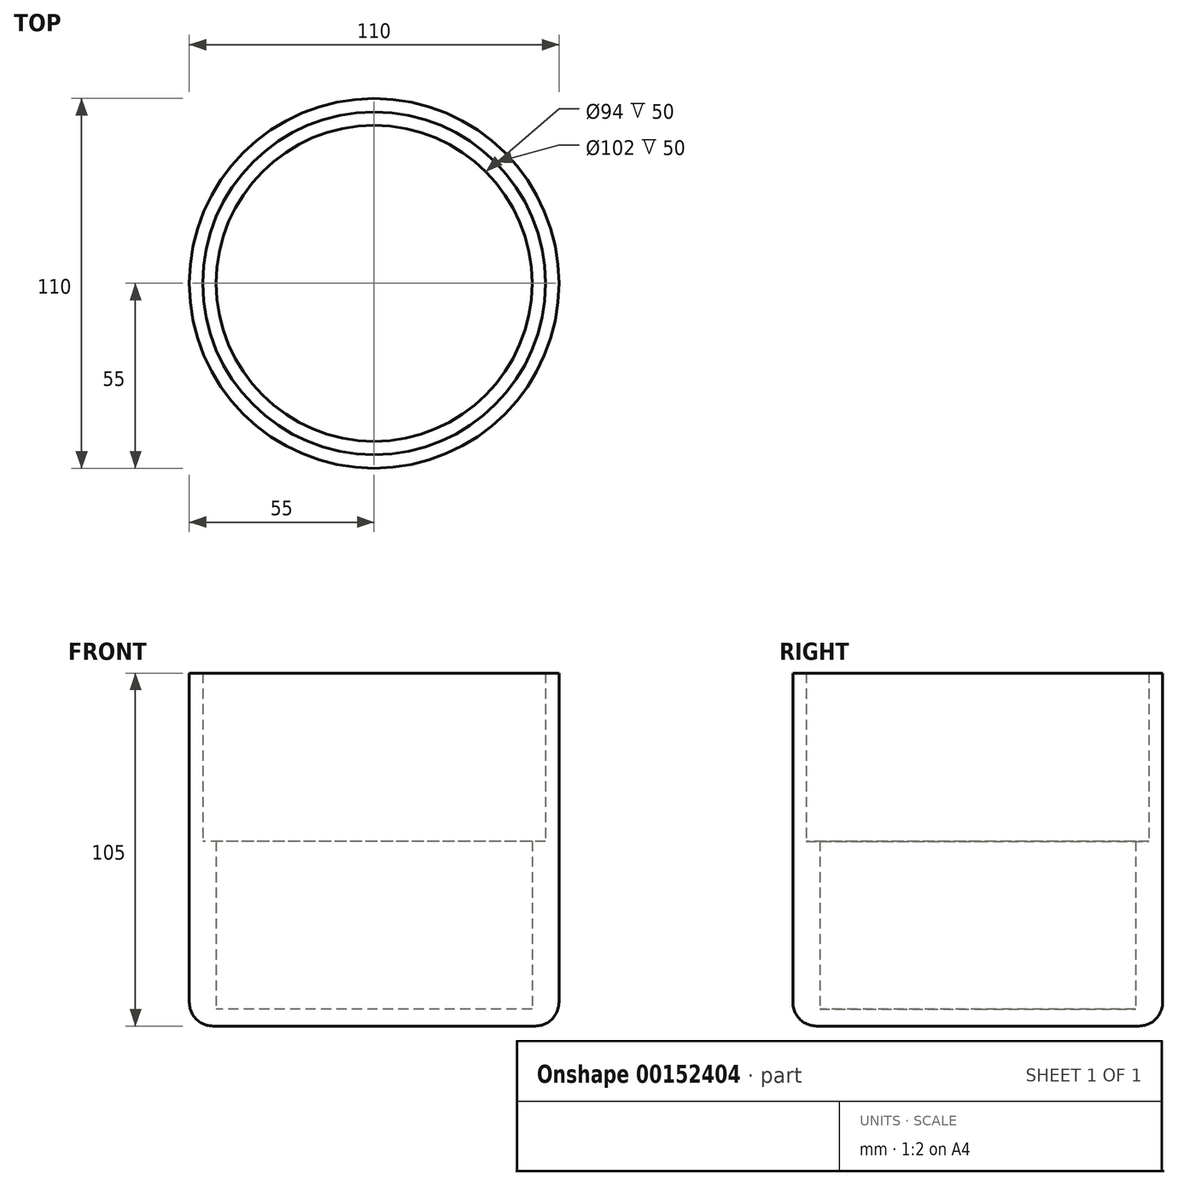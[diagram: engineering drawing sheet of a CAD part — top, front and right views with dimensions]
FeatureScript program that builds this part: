
annotation { "Feature Type Name" : "Feature", "Feature Type Description" : "" }
export const myFeature = defineFeature(function(context is Context, id is Id, definition is map)
    precondition{}
    {
        {
            var Q0;
            Q0=qCreatedBy(makeId("Top.planeOp"),FACE);
            var sketch = newSketch(context, id + "F0", { "sketchPlane" : qUnion([Q0])});
            skCircle(sketch, "E0", {"center": v(0, 0) * mm, "radius": 55 * mm});
            skCircle(sketch, "E1", {"center": v(0, 0) * mm, "radius": 51 * mm});
            skCircle(sketch, "E2", {"center": v(0, 0) * mm, "radius": 47 * mm});
            skSolve(sketch);
        }
        {
            var Q0;
            Q0 = qSketchRegion(id + "F0", true);
            var Q1;
            Q1=makeQuery(id+"F0.imprint","IMPRINT",FACE,{"disambiguationData":[TD([[makeQuery(id+"F0.imprint","IMPRINT",EDGE,{"derivedFrom":sQuery(id+"F0.wireOp",EDGE,"E1")}),1.0]])]});
            var Q2;
            Q2=makeQuery(id+"F0.imprint","IMPRINT",FACE,{"disambiguationData":[TD([[makeQuery(id+"F0.imprint","IMPRINT",EDGE,{"derivedFrom":sQuery(id+"F0.wireOp",EDGE,"E2")}),1.0]])]});
            extrude(context, id + "F1", {"entities" : qUnion([Q0, Q1, Q2]), "oppositeDirection" : true, "depth" : 5 * mm});
        }
        {
            var Q0;
            Q0=makeQuery(id+"F0.imprint","IMPRINT",FACE,{"disambiguationData":[TD([[makeQuery(id+"F0.imprint","IMPRINT",EDGE,{"derivedFrom":sQuery(id+"F0.wireOp",EDGE,"E1")}),1.0]])]});
            extrude(context, id + "F2", {"entities" : qUnion([Q0]), "operationType" : NewBodyOperationType.ADD, "depth" : 50 * mm});
        }
        {
            var Q0;
            Q0=makeQuery(id+"F0.imprint","IMPRINT",FACE,{"disambiguationData":[TD([[makeQuery(id+"F0.imprint","IMPRINT",EDGE,{"derivedFrom":sQuery(id+"F0.wireOp",EDGE,"E0")}),1.0]])]});
            extrude(context, id + "F3", {"entities" : qUnion([Q0]), "operationType" : NewBodyOperationType.ADD, "depth" : 100 * mm});
        }
        {
            var Q0;
            Q0=makeQuery(id+"F1.opExtrude","CAP_EDGE",EDGE,{"disambiguationData":[OSD([sQuery(id+"F0.wireOp",EDGE,"E0")])],"isStart":false});
            fillet(context, id + "F4", {"entities" : qUnion([Q0]), "radius" : 7 * mm, "tangentPropagation" : true, "allowEdgeOverflow" : false});
        }
    });
